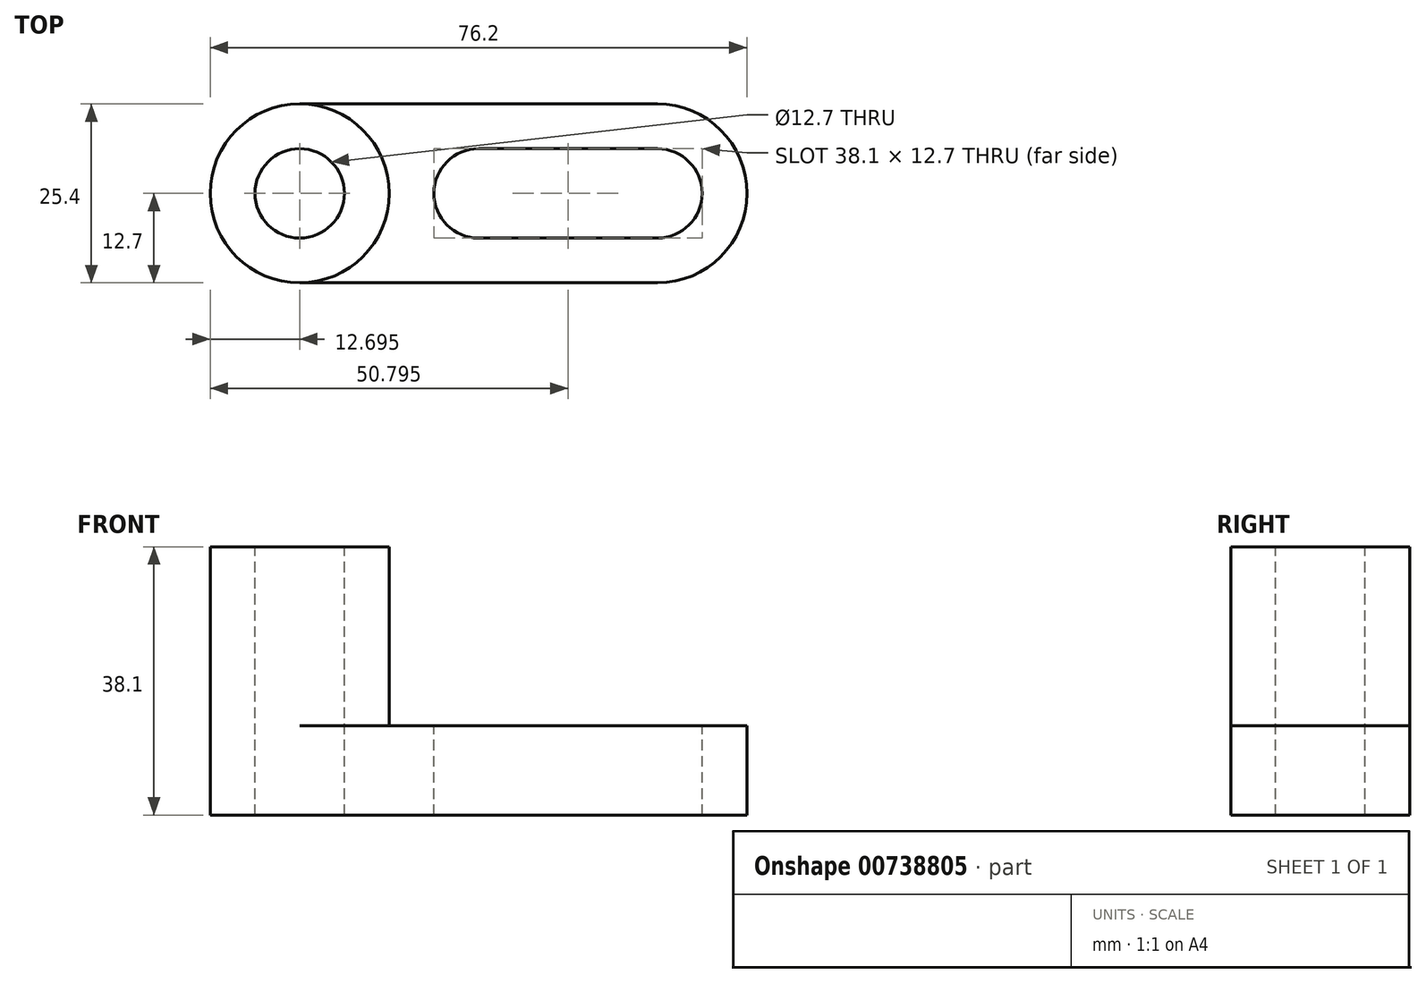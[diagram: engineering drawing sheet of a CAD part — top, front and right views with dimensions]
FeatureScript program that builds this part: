
annotation { "Feature Type Name" : "Feature", "Feature Type Description" : "" }
export const myFeature = defineFeature(function(context is Context, id is Id, definition is map)
    precondition{}
    {
        {
            var Q0;
            Q0=qCreatedBy(makeId("Front.planeOp"),FACE);
            var sketch = newSketch(context, id + "F0", { "sketchPlane" : qUnion([Q0])});
            skLineSegment(sketch, "E0.bottom", {"start": v(-42.92, 26.9) * mm, "end": v(33.28, 26.9) * mm});
            skLineSegment(sketch, "E0.top", {"start": v(-42.92, -11.2) * mm, "end": v(33.28, -11.2) * mm});
            skLineSegment(sketch, "E0.left", {"start": v(-42.92, 26.9) * mm, "end": v(-42.92, -11.2) * mm});
            skLineSegment(sketch, "E0.right", {"start": v(33.28, 26.9) * mm, "end": v(33.28, -11.2) * mm});
            skSolve(sketch);
        }
        {
            var Q0;
            Q0 = qSketchRegion(id + "F0", true);
            extrude(context, id + "F1", {"entities" : qUnion([Q0]), "depth" : 25.4 * mm, "offsetDistance" : 25.4 * mm});
        }
        {
            var Q0;
            Q0=makeQuery(id+"F1.opExtrude","CAP_FACE",FACE,{"disambiguationData":[OSD([sQuery(id+"F0.wireOp",EDGE,"E0.bottom"),sQuery(id+"F0.wireOp",EDGE,"E0.top"),sQuery(id+"F0.wireOp",EDGE,"E0.left"),sQuery(id+"F0.wireOp",EDGE,"E0.right")])],"isStart":false});
            var sketch = newSketch(context, id + "F2", { "sketchPlane" : qUnion([Q0])});
            skLineSegment(sketch, "E1", {"start": v(-17.52, 26.9) * mm, "end": v(-17.52, 1.5) * mm});
            skLineSegment(sketch, "E2", {"start": v(-17.52, 1.5) * mm, "end": v(33.28, 1.5) * mm});
            skSolve(sketch);
        }
        {
            var Q0;
            Q0 = qSketchRegion(id + "F2", true);
            var Q1;
            {var subQ0=sQuery(id+"F2.wireOp",EDGE,"E1");Q1=makeQuery(id+"F2.imprint","IMPRINT",FACE,{"disambiguationData":[TD([[makeQuery(id+"F2.imprint","IMPRINT",EDGE,{"derivedFrom":subQ0}),1.0]])]});}
            extrude(context, id + "F3", {"entities" : qUnion([Q0, Q1]), "operationType" : NewBodyOperationType.REMOVE, "endBound" : BoundingType.THROUGH_ALL, "oppositeDirection" : true, "depth" : 25.4 * mm, "offsetDistance" : 25.4 * mm});
        }
        {
            var Q0;
            Q0=makeQuery(id+"F3.boolean.opBoolean","COPY",FACE,{"derivedFrom":makeQuery(id+"F3.opExtrude","SWEPT_FACE",FACE,{"disambiguationData":[OSD([sQuery(id+"F2.wireOp",EDGE,"E2")])]})});
            var sketch = newSketch(context, id + "F4", { "sketchPlane" : qUnion([Q0])});
            skLineSegment(sketch, "E3", {"start": v(-4.82, 0) * mm, "end": v(-4.82, -25.4) * mm});
            skLineSegment(sketch, "E4", {"start": v(20.58, 0) * mm, "end": v(20.58, -25.4) * mm});
            skLineSegment(sketch, "E5", {"start": v(-17.52, -6.35) * mm, "end": v(33.28, -6.35) * mm});
            skLineSegment(sketch, "E6", {"start": v(-17.52, -19.05) * mm, "end": v(33.28, -19.05) * mm});
            skCircle(sketch, "E7", {"center": v(-4.82, -12.7) * mm, "radius": 6.35 * mm});
            skCircle(sketch, "E8", {"center": v(20.58, -12.7) * mm, "radius": 6.35 * mm});
            skArc(sketch, "E9", {"start": v(20.58, -25.4) * mm, "mid": v(33.28, -12.7) * mm, "end": v(20.58, 0) * mm});
            skSolve(sketch);
        }
        {
            var Q0;
            {var subQ0=sQuery(id+"F4.wireOp",EDGE,"E7");var subQ1=sQuery(id+"F4.wireOp",EDGE,"E3");var subQ2=makeQuery(id+"F4.imprint","INTERSECT",VERTEX,{"derivedFrom":[subQ1,sQuery(id+"F4.wireOp",EDGE,"E5"),subQ0]});Q0=makeQuery(id+"F4.imprint","IMPRINT",FACE,{"disambiguationData":[TD([[makeQuery(id+"F4.imprint","IMPRINT",EDGE,{"disambiguationData":[TD([[subQ2,-1.0]])],"derivedFrom":subQ1}),-1.0]])]});}
            var Q1;
            {var subQ0=sQuery(id+"F4.wireOp",EDGE,"E7");var subQ1=sQuery(id+"F4.wireOp",EDGE,"E3");var subQ2=makeQuery(id+"F4.imprint","INTERSECT",VERTEX,{"derivedFrom":[subQ1,sQuery(id+"F4.wireOp",EDGE,"E5"),subQ0]});Q1=makeQuery(id+"F4.imprint","IMPRINT",FACE,{"disambiguationData":[TD([[makeQuery(id+"F4.imprint","IMPRINT",EDGE,{"disambiguationData":[TD([[subQ2,-1.0]])],"derivedFrom":subQ1}),1.0]])]});}
            var Q2;
            {var subQ0=sQuery(id+"F4.wireOp",EDGE,"E8");var subQ1=sQuery(id+"F4.wireOp",EDGE,"E4");var subQ2=makeQuery(id+"F4.imprint","INTERSECT",VERTEX,{"derivedFrom":[subQ1,sQuery(id+"F4.wireOp",EDGE,"E5"),subQ0]});Q2=makeQuery(id+"F4.imprint","IMPRINT",FACE,{"disambiguationData":[TD([[makeQuery(id+"F4.imprint","IMPRINT",EDGE,{"disambiguationData":[TD([[subQ2,-1.0]])],"derivedFrom":subQ1}),-1.0]])]});}
            var Q3;
            {var subQ0=sQuery(id+"F4.wireOp",EDGE,"E8");var subQ1=sQuery(id+"F4.wireOp",EDGE,"E4");var subQ2=makeQuery(id+"F4.imprint","INTERSECT",VERTEX,{"derivedFrom":[subQ1,sQuery(id+"F4.wireOp",EDGE,"E5"),subQ0]});Q3=makeQuery(id+"F4.imprint","IMPRINT",FACE,{"disambiguationData":[TD([[makeQuery(id+"F4.imprint","IMPRINT",EDGE,{"disambiguationData":[TD([[subQ2,-1.0]])],"derivedFrom":subQ1}),1.0]])]});}
            var Q4;
            {var subQ0=sQuery(id+"F4.wireOp",EDGE,"E7");var subQ1=sQuery(id+"F4.wireOp",EDGE,"E5");var subQ2=sQuery(id+"F4.wireOp",EDGE,"E3");var subQ3=makeQuery(id+"F4.imprint","INTERSECT",VERTEX,{"derivedFrom":[subQ2,subQ1,subQ0]});Q4=makeQuery(id+"F4.imprint","IMPRINT",FACE,{"disambiguationData":[TD([[makeQuery(id+"F4.imprint","IMPRINT",EDGE,{"disambiguationData":[TD([[subQ3,-1.0]])],"derivedFrom":subQ1}),-1.0]])]});}
            var Q5;
            {var subQ0=sQuery(id+"F4.wireOp",EDGE,"E5");var subQ5=sQuery(id+"F4.wireOp",EDGE,"E9");var subQ6=makeQuery(id+"F4.imprint","INTERSECT",VERTEX,{"derivedFrom":[subQ0,subQ5]});Q5=makeQuery(id+"F4.imprint","IMPRINT",FACE,{"disambiguationData":[TD([[makeQuery(id+"F4.imprint","IMPRINT",EDGE,{"disambiguationData":[TD([[subQ6,-1.0]])],"derivedFrom":subQ0}),1.0]])]});}
            var Q6;
            {var subQ0=sQuery(id+"F4.wireOp",EDGE,"E6");var subQ4=sQuery(id+"F4.wireOp",EDGE,"E9");var subQ5=makeQuery(id+"F4.imprint","INTERSECT",VERTEX,{"derivedFrom":[subQ0,subQ4]});Q6=makeQuery(id+"F4.imprint","IMPRINT",FACE,{"disambiguationData":[TD([[makeQuery(id+"F4.imprint","IMPRINT",EDGE,{"disambiguationData":[TD([[subQ5,-1.0]])],"derivedFrom":subQ0}),-1.0]])]});}
            var Q7;
            {var subQ0=sQuery(id+"F4.wireOp",EDGE,"E6");var subQ3=sQuery(id+"F4.wireOp",EDGE,"E9");var subQ4=makeQuery(id+"F4.imprint","INTERSECT",VERTEX,{"derivedFrom":[subQ0,subQ3]});Q7=makeQuery(id+"F4.imprint","IMPRINT",FACE,{"disambiguationData":[TD([[makeQuery(id+"F4.imprint","IMPRINT",EDGE,{"disambiguationData":[TD([[subQ4,-1.0]])],"derivedFrom":subQ0}),1.0]])]});}
            var Q8;
            {var subQ0=sQuery(id+"F4.wireOp",EDGE,"E5");var subQ3=sQuery(id+"F4.wireOp",EDGE,"E9");var subQ4=makeQuery(id+"F4.imprint","INTERSECT",VERTEX,{"derivedFrom":[subQ0,subQ3]});Q8=makeQuery(id+"F4.imprint","IMPRINT",FACE,{"disambiguationData":[TD([[makeQuery(id+"F4.imprint","IMPRINT",EDGE,{"disambiguationData":[TD([[subQ4,-1.0]])],"derivedFrom":subQ0}),-1.0]])]});}
            extrude(context, id + "F5", {"entities" : qUnion([Q0, Q1, Q2, Q3, Q4, Q5, Q6, Q7, Q8]), "operationType" : NewBodyOperationType.REMOVE, "endBound" : BoundingType.THROUGH_ALL, "oppositeDirection" : true, "depth" : 25.4 * mm, "offsetDistance" : 25.4 * mm});
        }
        {
            var Q0;
            Q0=makeQuery(id+"F1.opExtrude","SWEPT_FACE",FACE,{"disambiguationData":[OSD([sQuery(id+"F0.wireOp",EDGE,"E0.bottom")])]});
            var sketch = newSketch(context, id + "F6", { "sketchPlane" : qUnion([Q0])});
            skLineSegment(sketch, "E10", {"start": v(-42.92, -12.7) * mm, "end": v(-17.52, -12.7) * mm});
            skLineSegment(sketch, "E11", {"start": v(-30.22, -25.4) * mm, "end": v(-30.22, 0) * mm});
            skCircle(sketch, "E12", {"center": v(-30.22, -12.7) * mm, "radius": 6.35 * mm});
            skCircle(sketch, "E13", {"center": v(-30.22, -12.7) * mm, "radius": 12.7 * mm});
            skSolve(sketch);
        }
        {
            var Q0;
            {var subQ1=sQuery(id+"F0.wireOp",EDGE,"E0.bottom");var subQ2=makeQuery(id+"F3.boolean.opBoolean","COPY",EDGE,{"derivedFrom":makeQuery(id+"F3.opExtrude","SWEPT_EDGE",EDGE,{"disambiguationData":[OSD([subQ1,sQuery(id+"F2.wireOp",EDGE,"E1")])]})});var subQ4=makeQuery(id+"F1.opExtrude","CAP_EDGE",EDGE,{"disambiguationData":[OSD([subQ1])],"isStart":false});var subQ6=makeQuery(id+"F6.imprint","INTERSECT",VERTEX,{"derivedFrom":[subQ2,subQ4]});Q0=makeQuery(id+"F6.imprint","IMPRINT",FACE,{"disambiguationData":[TD([[makeQuery(id+"F6.imprint","IMPRINT",EDGE,{"disambiguationData":[TD([[subQ6,1.0]])],"derivedFrom":subQ4}),1.0]])]});}
            var Q1;
            {var subQ1=sQuery(id+"F0.wireOp",EDGE,"E0.bottom");var subQ2=makeQuery(id+"F3.boolean.opBoolean","COPY",EDGE,{"derivedFrom":makeQuery(id+"F3.opExtrude","SWEPT_EDGE",EDGE,{"disambiguationData":[OSD([subQ1,sQuery(id+"F2.wireOp",EDGE,"E1")])]})});var subQ4=makeQuery(id+"F1.opExtrude","CAP_EDGE",EDGE,{"disambiguationData":[OSD([subQ1])],"isStart":true});var subQ6=makeQuery(id+"F6.imprint","INTERSECT",VERTEX,{"derivedFrom":[subQ2,subQ4]});Q1=makeQuery(id+"F6.imprint","IMPRINT",FACE,{"disambiguationData":[TD([[makeQuery(id+"F6.imprint","IMPRINT",EDGE,{"disambiguationData":[TD([[subQ6,1.0]])],"derivedFrom":subQ4}),-1.0]])]});}
            var Q2;
            {var subQ1=sQuery(id+"F0.wireOp",EDGE,"E0.bottom");var subQ2=makeQuery(id+"F1.opExtrude","SWEPT_EDGE",EDGE,{"disambiguationData":[OSD([subQ1,sQuery(id+"F0.wireOp",EDGE,"E0.left")])]});var subQ4=makeQuery(id+"F1.opExtrude","CAP_EDGE",EDGE,{"disambiguationData":[OSD([subQ1])],"isStart":true});var subQ6=makeQuery(id+"F6.imprint","INTERSECT",VERTEX,{"derivedFrom":[subQ2,subQ4]});Q2=makeQuery(id+"F6.imprint","IMPRINT",FACE,{"disambiguationData":[TD([[makeQuery(id+"F6.imprint","IMPRINT",EDGE,{"disambiguationData":[TD([[subQ6,-1.0]])],"derivedFrom":subQ4}),-1.0]])]});}
            var Q3;
            {var subQ1=sQuery(id+"F0.wireOp",EDGE,"E0.bottom");var subQ2=makeQuery(id+"F1.opExtrude","SWEPT_EDGE",EDGE,{"disambiguationData":[OSD([subQ1,sQuery(id+"F0.wireOp",EDGE,"E0.left")])]});var subQ4=makeQuery(id+"F1.opExtrude","CAP_EDGE",EDGE,{"disambiguationData":[OSD([subQ1])],"isStart":false});var subQ6=makeQuery(id+"F6.imprint","INTERSECT",VERTEX,{"derivedFrom":[subQ2,subQ4]});Q3=makeQuery(id+"F6.imprint","IMPRINT",FACE,{"disambiguationData":[TD([[makeQuery(id+"F6.imprint","IMPRINT",EDGE,{"disambiguationData":[TD([[subQ6,-1.0]])],"derivedFrom":subQ4}),1.0]])]});}
            var Q4;
            {var subQ0=sQuery(id+"F6.wireOp",EDGE,"E12");var subQ1=sQuery(id+"F6.wireOp",EDGE,"E10");var subQ2=makeQuery(id+"F6.imprint","INTERSECT",VERTEX,{"disambiguationData":[OD(0.0)],"derivedFrom":[subQ1,subQ0]});Q4=makeQuery(id+"F6.imprint","IMPRINT",FACE,{"disambiguationData":[TD([[makeQuery(id+"F6.imprint","IMPRINT",EDGE,{"disambiguationData":[TD([[subQ2,-1.0]])],"derivedFrom":subQ1}),-1.0]])]});}
            var Q5;
            {var subQ0=sQuery(id+"F6.wireOp",EDGE,"E11");var subQ1=sQuery(id+"F6.wireOp",EDGE,"E10");var subQ2=makeQuery(id+"F6.imprint","INTERSECT",VERTEX,{"derivedFrom":[subQ1,subQ0]});Q5=makeQuery(id+"F6.imprint","IMPRINT",FACE,{"disambiguationData":[TD([[makeQuery(id+"F6.imprint","IMPRINT",EDGE,{"disambiguationData":[TD([[subQ2,-1.0]])],"derivedFrom":subQ1}),-1.0]])]});}
            var Q6;
            {var subQ0=sQuery(id+"F6.wireOp",EDGE,"E11");var subQ1=sQuery(id+"F6.wireOp",EDGE,"E10");var subQ2=makeQuery(id+"F6.imprint","INTERSECT",VERTEX,{"derivedFrom":[subQ1,subQ0]});Q6=makeQuery(id+"F6.imprint","IMPRINT",FACE,{"disambiguationData":[TD([[makeQuery(id+"F6.imprint","IMPRINT",EDGE,{"disambiguationData":[TD([[subQ2,-1.0]])],"derivedFrom":subQ1}),1.0]])]});}
            var Q7;
            {var subQ0=sQuery(id+"F6.wireOp",EDGE,"E12");var subQ1=sQuery(id+"F6.wireOp",EDGE,"E10");var subQ2=makeQuery(id+"F6.imprint","INTERSECT",VERTEX,{"disambiguationData":[OD(0.0)],"derivedFrom":[subQ1,subQ0]});Q7=makeQuery(id+"F6.imprint","IMPRINT",FACE,{"disambiguationData":[TD([[makeQuery(id+"F6.imprint","IMPRINT",EDGE,{"disambiguationData":[TD([[subQ2,-1.0]])],"derivedFrom":subQ1}),1.0]])]});}
            extrude(context, id + "F7", {"entities" : qUnion([Q0, Q1, Q2, Q3, Q4, Q5, Q6, Q7]), "operationType" : NewBodyOperationType.REMOVE, "oppositeDirection" : true, "depth" : 25.4 * mm, "offsetDistance" : 25.4 * mm});
        }
        {
            var Q0;
            Q0=makeQuery(id+"F7.boolean.opBoolean","COPY",FACE,{"derivedFrom":makeQuery(id+"F7.opExtrude","CAP_FACE",FACE,{"disambiguationData":[OSD([sQuery(id+"F6.wireOp",EDGE,"E12")])],"isStart":false})});
            var Q1;
            {var subQ0=sQuery(id+"F0.wireOp",EDGE,"E0.bottom");var subQ1=makeQuery(id+"F1.opExtrude","CAP_EDGE",EDGE,{"disambiguationData":[OSD([subQ0])],"isStart":false});var subQ2=sQuery(id+"F0.wireOp",EDGE,"E0.left");var subQ3=makeQuery(id+"F1.opExtrude","SWEPT_EDGE",EDGE,{"disambiguationData":[OSD([subQ0,subQ2])]});var subQ4=makeQuery(id+"F6.imprint","INTERSECT",VERTEX,{"derivedFrom":[subQ3,subQ1]});var subQ5=sQuery(id+"F6.wireOp",EDGE,"E13");var subQ6=makeQuery(id+"F6.imprint","INTERSECT",VERTEX,{"derivedFrom":[subQ1,sQuery(id+"F6.wireOp",EDGE,"E11"),subQ5]});Q1=makeQuery(id+"F7.boolean.opBoolean","COPY",FACE,{"derivedFrom":makeQuery(id+"F7.opExtrude","CAP_FACE",FACE,{"disambiguationData":[OSD([subQ0,subQ2,subQ5]),TDD([makeQuery(id+"F6.imprint","IMPRINT",EDGE,{"disambiguationData":[TD([[subQ6,1.0]])],"derivedFrom":subQ5}),makeQuery(id+"F6.imprint","IMPRINT",EDGE,{"disambiguationData":[TD([[subQ4,-1.0]])],"derivedFrom":subQ3}),makeQuery(id+"F6.imprint","IMPRINT",EDGE,{"disambiguationData":[TD([[subQ4,-1.0]])],"derivedFrom":subQ1})])],"isStart":false})});}
            var Q2;
            {var subQ0=sQuery(id+"F0.wireOp",EDGE,"E0.bottom");var subQ1=makeQuery(id+"F1.opExtrude","CAP_EDGE",EDGE,{"disambiguationData":[OSD([subQ0])],"isStart":true});var subQ2=sQuery(id+"F0.wireOp",EDGE,"E0.left");var subQ3=makeQuery(id+"F1.opExtrude","SWEPT_EDGE",EDGE,{"disambiguationData":[OSD([subQ0,subQ2])]});var subQ4=makeQuery(id+"F6.imprint","INTERSECT",VERTEX,{"derivedFrom":[subQ3,subQ1]});var subQ5=sQuery(id+"F6.wireOp",EDGE,"E13");var subQ6=makeQuery(id+"F6.imprint","INTERSECT",VERTEX,{"derivedFrom":[subQ1,sQuery(id+"F6.wireOp",EDGE,"E11"),subQ5]});Q2=makeQuery(id+"F7.boolean.opBoolean","COPY",FACE,{"derivedFrom":makeQuery(id+"F7.opExtrude","CAP_FACE",FACE,{"disambiguationData":[OSD([subQ0,subQ2,subQ5]),TDD([makeQuery(id+"F6.imprint","IMPRINT",EDGE,{"disambiguationData":[TD([[subQ6,-1.0]])],"derivedFrom":subQ5}),makeQuery(id+"F6.imprint","IMPRINT",EDGE,{"disambiguationData":[TD([[subQ4,1.0]])],"derivedFrom":subQ3}),makeQuery(id+"F6.imprint","IMPRINT",EDGE,{"disambiguationData":[TD([[subQ4,-1.0]])],"derivedFrom":subQ1})])],"isStart":false})});}
            extrude(context, id + "F8", {"entities" : qUnion([Q0, Q1, Q2]), "operationType" : NewBodyOperationType.REMOVE, "endBound" : BoundingType.THROUGH_ALL, "oppositeDirection" : true, "depth" : 25.4 * mm, "offsetDistance" : 25.4 * mm});
        }
    });
